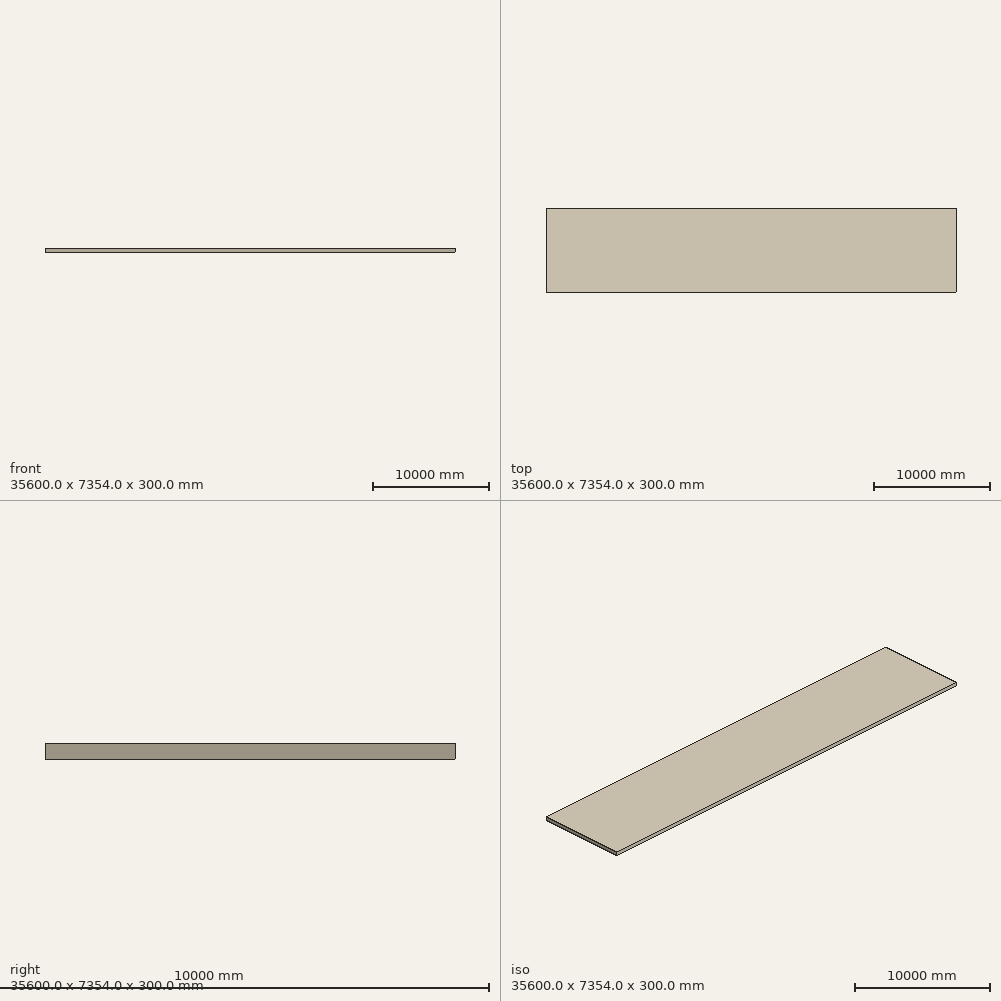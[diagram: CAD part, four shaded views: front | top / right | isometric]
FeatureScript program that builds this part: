
annotation { "Feature Type Name" : "Feature", "Feature Type Description" : "" }
export const myFeature = defineFeature(function(context is Context, id is Id, definition is map)
    precondition{}
    {
        {
            var Q0;
            Q0=qCreatedBy(makeId("Top.planeOp"),FACE);
            var sketch = newSketch(context, id + "F0", { "sketchPlane" : qUnion([Q0])});
            skLineSegment(sketch, "E0.bottom", {"start": v(17800, -3677) * mm, "end": v(-17800, -3677) * mm});
            skLineSegment(sketch, "E0.top", {"start": v(17800, 3677) * mm, "end": v(-17800, 3677) * mm});
            skLineSegment(sketch, "E0.left", {"start": v(17800, -3677) * mm, "end": v(17800, 3677) * mm});
            skLineSegment(sketch, "E0.right", {"start": v(-17800, -3677) * mm, "end": v(-17800, 3677) * mm});
            skPoint(sketch, "E0.middle", {"position": v(0, 0) * mm});
            skSolve(sketch);
        }
        {
            var Q0;
            Q0 = qSketchRegion(id + "F0", true);
            extrude(context, id + "F1", {"entities" : qUnion([Q0]), "oppositeDirection" : true, "depth" : 300 * mm, "offsetDistance" : 25 * mm});
        }
    });
